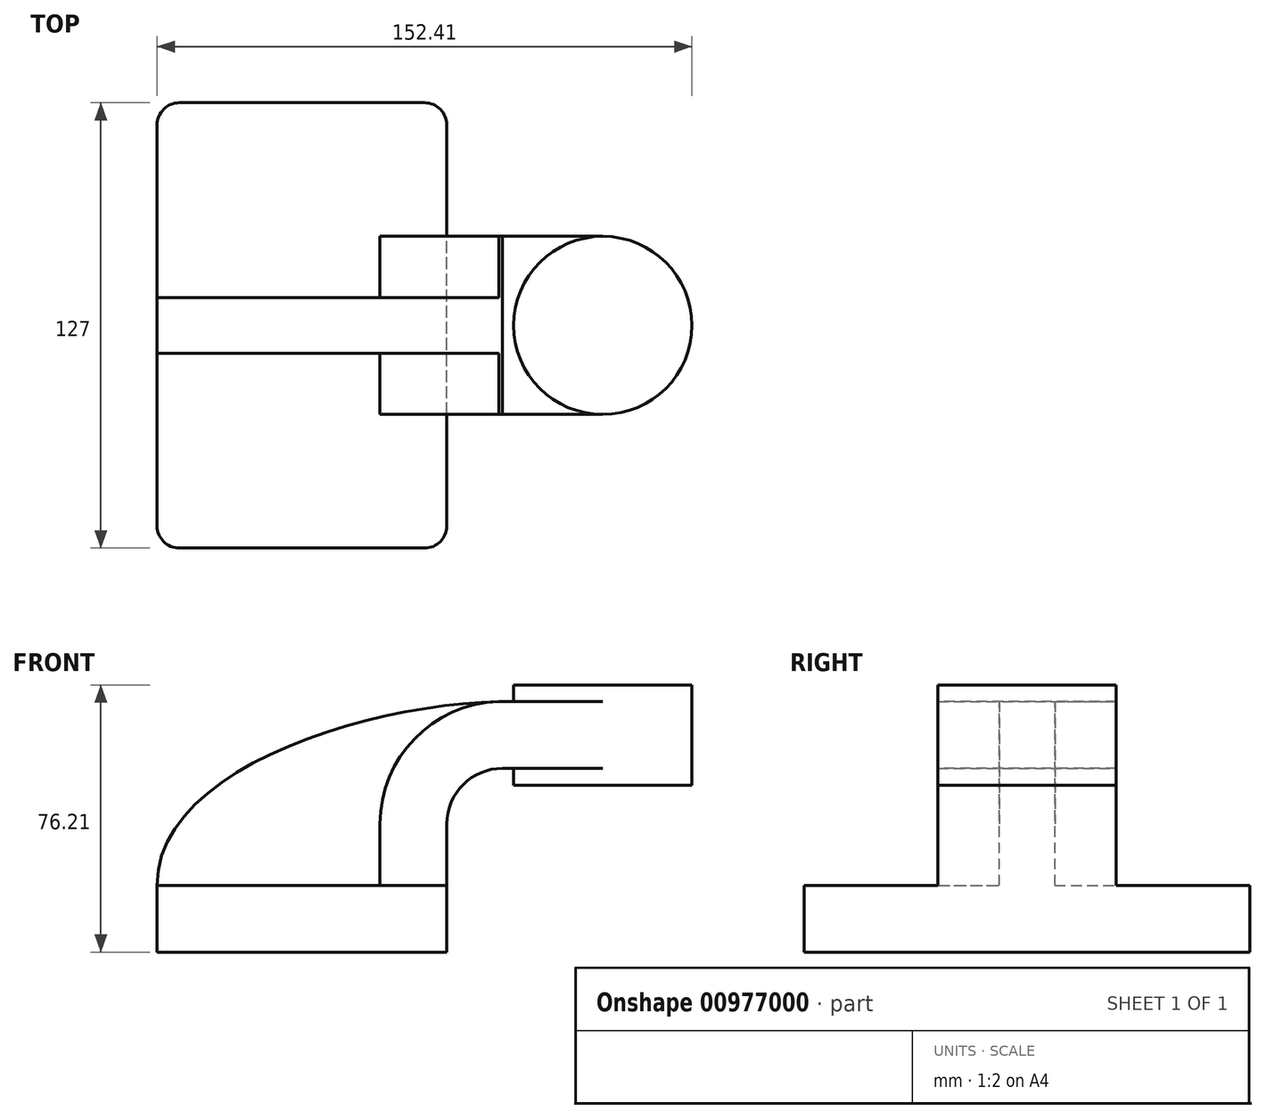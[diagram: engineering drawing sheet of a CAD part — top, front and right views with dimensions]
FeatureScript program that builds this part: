
annotation { "Feature Type Name" : "Feature", "Feature Type Description" : "" }
export const myFeature = defineFeature(function(context is Context, id is Id, definition is map)
    precondition{}
    {
        {
            var Q0;
            Q0=qCreatedBy(makeId("Front.planeOp"),FACE);
            var sketch = newSketch(context, id + "F0", { "sketchPlane" : qUnion([Q0])});
            skLineSegment(sketch, "E0.bottom", {"start": v(-41.28, 9.52) * mm, "end": v(41.27, 9.53) * mm});
            skLineSegment(sketch, "E0.top", {"start": v(-41.28, -9.53) * mm, "end": v(41.28, -9.53) * mm});
            skLineSegment(sketch, "E0.left", {"start": v(-41.28, 9.52) * mm, "end": v(-41.27, -9.53) * mm});
            skLineSegment(sketch, "E0.right", {"start": v(41.28, 9.53) * mm, "end": v(41.28, -9.52) * mm});
            skPoint(sketch, "E0.middle", {"position": v(0, 0) * mm});
            skLineSegment(sketch, "E1.bottom", {"start": v(60.32, 38.1) * mm, "end": v(111.12, 38.1) * mm});
            skLineSegment(sketch, "E1.top", {"start": v(60.32, 66.67) * mm, "end": v(111.12, 66.67) * mm});
            skLineSegment(sketch, "E1.left", {"start": v(60.32, 38.1) * mm, "end": v(60.32, 66.67) * mm});
            skLineSegment(sketch, "E1.right", {"start": v(111.12, 38.1) * mm, "end": v(111.12, 66.67) * mm});
            skPoint(sketch, "E1.middle", {"position": v(85.72, 52.39) * mm});
            skLineSegment(sketch, "E2", {"start": v(41.27, 9.53) * mm, "end": v(41.27, 27) * mm});
            skArc(sketch, "E3", {"start": v(41.27, 27) * mm, "mid": v(45.92, 38.23) * mm, "end": v(57.15, 42.88) * mm});
            skLineSegment(sketch, "E4", {"start": v(57.15, 42.88) * mm, "end": v(85.72, 42.88) * mm});
            skLineSegment(sketch, "E5.0", {"start": v(57.15, 61.93) * mm, "end": v(85.72, 61.93) * mm});
            skArc(sketch, "E5.1", {"start": v(22.22, 27) * mm, "mid": v(32.45, 51.7) * mm, "end": v(57.15, 61.93) * mm});
            skLineSegment(sketch, "E5.2", {"start": v(22.22, 9.53) * mm, "end": v(22.22, 27) * mm});
            skPoint(sketch, "E6.endSnap0", {"position": v(85.72, 66.67) * mm});
            skFitSpline(sketch, "E7", {"points": [v(-41.28, 9.52) * mm, v(57.15, 61.93) * mm], "startDerivative": vector(-0.18, 101.7) * mm, "endDerivative": vector(110.52, 1.24) * mm});
            skLineSegment(sketch, "E8", {"start": v(85.72, 66.67) * mm, "end": v(85.72, 38.1) * mm});
            skSolve(sketch);
        }
        {
            var Q0;
            Q0=makeQuery(id+"F0.imprint","IMPRINT",FACE,{"disambiguationData":[TD([[makeQuery(id+"F0.imprint","IMPRINT",EDGE,{"derivedFrom":sQuery(id+"F0.wireOp",EDGE,"E0.top")}),1.0]])]});
            extrude(context, id + "F1", {"entities" : qUnion([Q0]), "endBound" : BoundingType.SYMMETRIC, "depth" : 127 * mm, "offsetDistance" : 25.4 * mm});
        }
        {
            var Q0;
            {var subQ1=sQuery(id+"F0.wireOp",EDGE,"E2");Q0=makeQuery(id+"F0.imprint","IMPRINT",FACE,{"disambiguationData":[TD([[makeQuery(id+"F0.imprint","IMPRINT",EDGE,{"derivedFrom":subQ1}),1.0]])]});}
            var Q1;
            {var subQ0=sQuery(id+"F0.wireOp",EDGE,"E4");var subQ1=sQuery(id+"F0.wireOp",EDGE,"E1.left");var subQ2=makeQuery(id+"F0.imprint","INTERSECT",VERTEX,{"derivedFrom":[subQ1,subQ0]});Q1=makeQuery(id+"F0.imprint","IMPRINT",FACE,{"disambiguationData":[TD([[makeQuery(id+"F0.imprint","IMPRINT",EDGE,{"disambiguationData":[TD([[subQ2,-1.0]])],"derivedFrom":subQ1}),-1.0]])]});}
            extrude(context, id + "F2", {"entities" : qUnion([Q0, Q1]), "operationType" : NewBodyOperationType.ADD, "endBound" : BoundingType.SYMMETRIC, "depth" : 50.8 * mm, "offsetDistance" : 25.4 * mm});
        }
        {
            var Q0;
            {var subQ3=sQuery(id+"F0.wireOp",EDGE,"E5.2");Q0=makeQuery(id+"F0.imprint","IMPRINT",FACE,{"disambiguationData":[TD([[makeQuery(id+"F0.imprint","IMPRINT",EDGE,{"derivedFrom":subQ3}),1.0]])]});}
            extrude(context, id + "F3", {"entities" : qUnion([Q0]), "operationType" : NewBodyOperationType.ADD, "endBound" : BoundingType.SYMMETRIC, "depth" : 15.88 * mm, "offsetDistance" : 25.4 * mm});
        }
        {
            var Q0;
            {var subQ4=sQuery(id+"F0.wireOp",EDGE,"E1.right");Q0=makeQuery(id+"F0.imprint","IMPRINT",FACE,{"disambiguationData":[TD([[makeQuery(id+"F0.imprint","IMPRINT",EDGE,{"derivedFrom":subQ4}),1.0]])]});}
            var Q1;
            Q1=sQuery(id+"F0.wireOp",EDGE,"E8");
            revolve(context, id + "F4", {"operationType" : NewBodyOperationType.ADD, "surfaceOperationType" : NewSurfaceOperationType.NEW, "entities" : qUnion([Q0]), "axis" : qUnion([Q1]), "revolveType" : RevolveType.FULL});
        }
        {
            var Q0;
            Q0=makeQuery(id+"F1.opExtrude","CAP_EDGE",EDGE,{"disambiguationData":[OSD([sQuery(id+"F0.wireOp",EDGE,"E0.right")])],"isStart":false});
            var Q1;
            Q1=makeQuery(id+"F1.opExtrude","CAP_EDGE",EDGE,{"disambiguationData":[OSD([sQuery(id+"F0.wireOp",EDGE,"E0.left")])],"isStart":false});
            var Q2;
            Q2=makeQuery(id+"F1.opExtrude","CAP_EDGE",EDGE,{"disambiguationData":[OSD([sQuery(id+"F0.wireOp",EDGE,"E0.right")])],"isStart":true});
            var Q3;
            Q3=makeQuery(id+"F1.opExtrude","CAP_EDGE",EDGE,{"disambiguationData":[OSD([sQuery(id+"F0.wireOp",EDGE,"E0.left")])],"isStart":true});
            fillet(context, id + "F5", {"entities" : qUnion([Q0, Q1, Q2, Q3]), "radius" : 6.35 * mm, "tangentPropagation" : true, "allowEdgeOverflow" : false});
        }
    });
